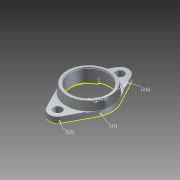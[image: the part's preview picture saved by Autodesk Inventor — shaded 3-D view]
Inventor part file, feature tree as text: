
AUTODESK INVENTOR PART (.ipt)
format: ipt  version: 2015 (Build 190159000, 159)  size: 466,432 bytes
history: native  units: in
note: dims shown in document units (in); Inventor stores cm internally (conversion verified against a paired STEP export)
features: projected_geometry x2, other x1, sketch x1, imported_body x1
ambient origin geometry x8: Origin, YZ Plane, XZ Plane, XY Plane, X Axis, Y Axis, Z Axis, Center Point
bodies: Solid1 (feature_tree)
feature tree (5):
  other  "KFL08.ipt1"
  sketch  "Sketch1"  dims[d0=0.1024in d1=0.1024in d2=0.4331in d3=0.7185in]
  imported_body  "Base1"
  projected_geometry  "Projected Loop1"
  projected_geometry  "Projected Loop2"
